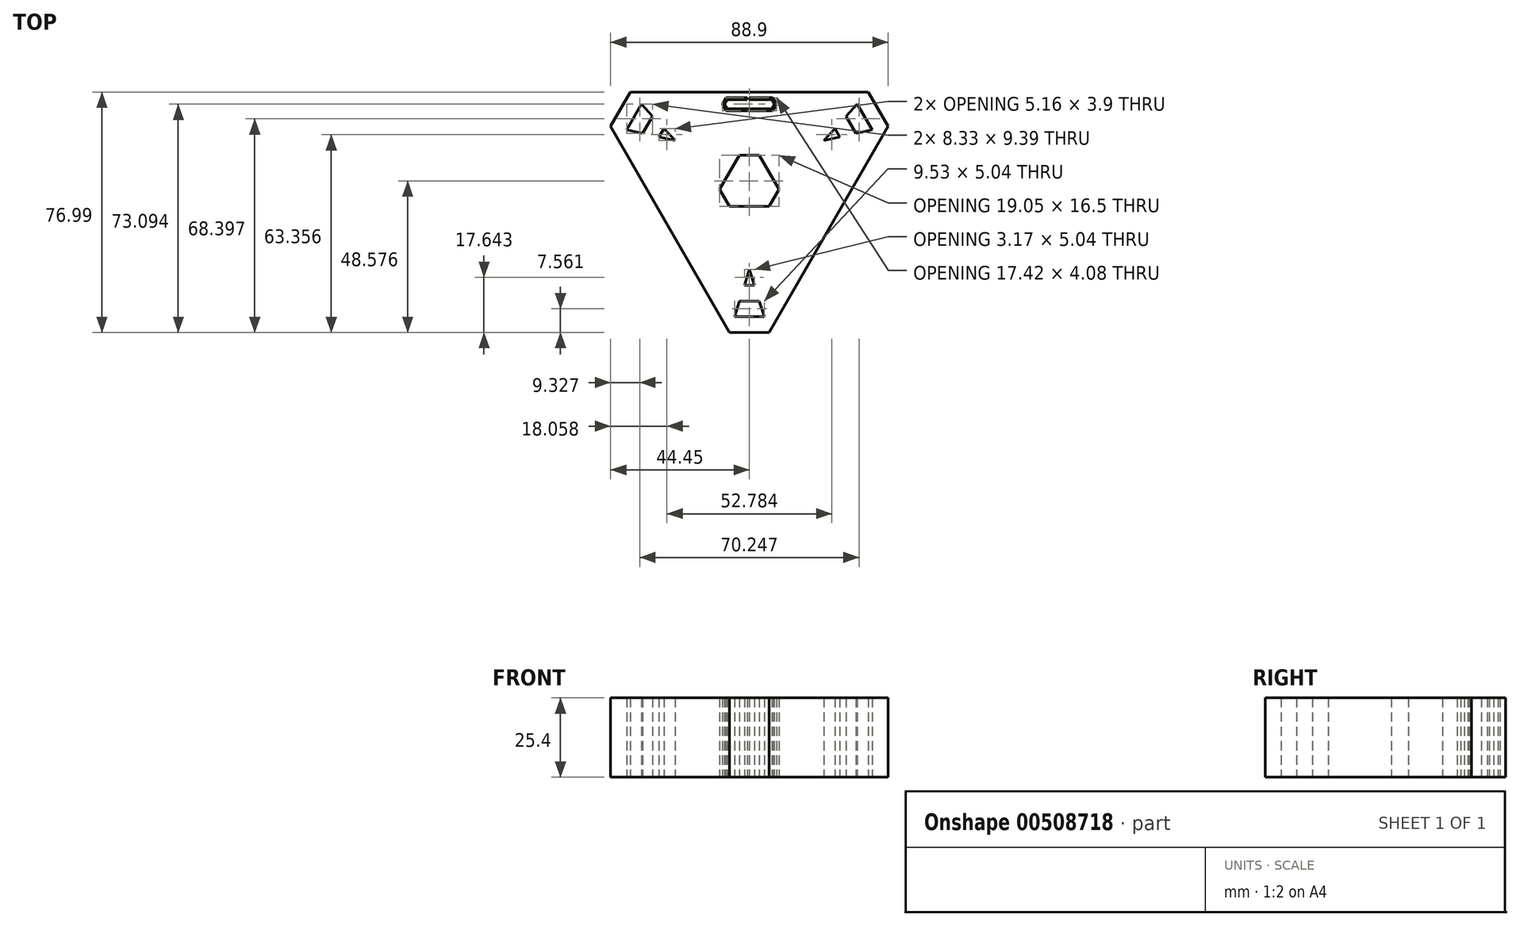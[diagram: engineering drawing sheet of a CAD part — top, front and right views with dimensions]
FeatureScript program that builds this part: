
annotation { "Feature Type Name" : "Feature", "Feature Type Description" : "" }
export const myFeature = defineFeature(function(context is Context, id is Id, definition is map)
    precondition{}
    {
        {
            var Q0;
            Q0=qCreatedBy(makeId("Top.planeOp"),FACE);
            var sketch = newSketch(context, id + "F0", { "sketchPlane" : qUnion([Q0])});
            skCircle(sketch, "E0.cCircle", {"center": v(0, 0) * mm, "radius": 29.33 * mm, "construction": true});
            skLineSegment(sketch, "E0.0", {"start": v(-50.8, 29.33) * mm, "end": v(50.8, 29.33) * mm, "construction": true});
            skLineSegment(sketch, "E0.1", {"start": v(50.8, 29.33) * mm, "end": v(0, -58.66) * mm, "construction": true});
            skLineSegment(sketch, "E0.2", {"start": v(0, -58.66) * mm, "end": v(-50.8, 29.33) * mm, "construction": true});
            skPoint(sketch, "E0.0.midPoint", {"position": v(0, 29.33) * mm});
            skPoint(sketch, "E1", {"position": v(-25.4, -14.66) * mm});
            skPoint(sketch, "E2", {"position": v(25.4, -14.66) * mm});
            skSolve(sketch);
        }
        {
            var Q0;
            Q0=qCreatedBy(makeId("Top.planeOp"),FACE);
            var sketch = newSketch(context, id + "F1", { "sketchPlane" : qUnion([Q0])});
            skPoint(sketch, "E3.0", {"position": v(0, 29.33) * mm});
            skPoint(sketch, "E4.0", {"position": v(-50.8, 29.33) * mm});
            skPoint(sketch, "E5.0", {"position": v(-25.4, -14.66) * mm});
            skPoint(sketch, "E6.0", {"position": v(25.4, -14.66) * mm});
            skPoint(sketch, "E7.0", {"position": v(50.8, 29.33) * mm});
            skPoint(sketch, "E8.0", {"position": v(0, -58.66) * mm});
            skLineSegment(sketch, "E9", {"start": v(-50.8, 29.33) * mm, "end": v(0, 29.33) * mm, "construction": true});
            skLineSegment(sketch, "E10", {"start": v(-50.8, 29.33) * mm, "end": v(-25.4, -14.66) * mm, "construction": true});
            skLineSegment(sketch, "E11", {"start": v(-25.4, -14.66) * mm, "end": v(0, 29.33) * mm, "construction": true});
            skLineSegment(sketch, "E12", {"start": v(0, 29.33) * mm, "end": v(50.8, 29.33) * mm, "construction": true});
            skLineSegment(sketch, "E13", {"start": v(50.8, 29.33) * mm, "end": v(25.4, -14.66) * mm, "construction": true});
            skLineSegment(sketch, "E14", {"start": v(25.4, -14.66) * mm, "end": v(0, 29.33) * mm, "construction": true});
            skLineSegment(sketch, "E15", {"start": v(0, -58.66) * mm, "end": v(-25.4, -14.66) * mm, "construction": true});
            skLineSegment(sketch, "E16", {"start": v(-25.4, -14.66) * mm, "end": v(25.4, -14.66) * mm, "construction": true});
            skLineSegment(sketch, "E17", {"start": v(25.4, -14.66) * mm, "end": v(0, -58.66) * mm, "construction": true});
            skPoint(sketch, "E18", {"position": v(-25.4, 29.33) * mm});
            skPoint(sketch, "E19", {"position": v(-38.1, 7.33) * mm});
            skPoint(sketch, "E20", {"position": v(-12.7, 7.33) * mm});
            skPoint(sketch, "E21", {"position": v(12.7, 7.33) * mm});
            skPoint(sketch, "E22", {"position": v(38.1, 7.33) * mm});
            skPoint(sketch, "E23", {"position": v(25.4, 29.33) * mm});
            skPoint(sketch, "E24", {"position": v(0, -14.66) * mm});
            skPoint(sketch, "E25", {"position": v(-12.7, -36.66) * mm});
            skPoint(sketch, "E26", {"position": v(12.7, -36.66) * mm});
            skSolve(sketch);
        }
        {
            var Q0;
            Q0=qCreatedBy(makeId("Top.planeOp"),FACE);
            var sketch = newSketch(context, id + "F2", { "sketchPlane" : qUnion([Q0])});
            skPoint(sketch, "E27.0", {"position": v(-25.4, 29.33) * mm});
            skPoint(sketch, "E28.0", {"position": v(-38.1, 7.33) * mm});
            skPoint(sketch, "E29.0", {"position": v(-50.8, 29.33) * mm});
            skPoint(sketch, "E30.0", {"position": v(25.4, 29.33) * mm});
            skPoint(sketch, "E31.0", {"position": v(50.8, 29.33) * mm});
            skPoint(sketch, "E32.0", {"position": v(38.1, 7.33) * mm});
            skPoint(sketch, "E33.0", {"position": v(12.7, -36.66) * mm});
            skPoint(sketch, "E34.0", {"position": v(-12.7, -36.66) * mm});
            skPoint(sketch, "E35.0", {"position": v(0, -58.66) * mm});
            skLineSegment(sketch, "E36", {"start": v(-38.1, 7.33) * mm, "end": v(-25.4, 29.33) * mm, "construction": true});
            skLineSegment(sketch, "E37", {"start": v(-50.8, 29.33) * mm, "end": v(-25.4, 29.33) * mm, "construction": true});
            skLineSegment(sketch, "E38", {"start": v(-50.8, 29.33) * mm, "end": v(-38.1, 7.33) * mm, "construction": true});
            skLineSegment(sketch, "E39", {"start": v(25.4, 29.33) * mm, "end": v(50.8, 29.33) * mm, "construction": true});
            skLineSegment(sketch, "E40", {"start": v(50.8, 29.33) * mm, "end": v(38.1, 7.33) * mm, "construction": true});
            skLineSegment(sketch, "E41", {"start": v(38.1, 7.33) * mm, "end": v(25.4, 29.33) * mm, "construction": true});
            skLineSegment(sketch, "E42", {"start": v(-12.7, -36.66) * mm, "end": v(0, -58.66) * mm, "construction": true});
            skLineSegment(sketch, "E43", {"start": v(12.7, -36.66) * mm, "end": v(-12.7, -36.66) * mm, "construction": true});
            skLineSegment(sketch, "E44", {"start": v(0, -58.66) * mm, "end": v(12.7, -36.66) * mm, "construction": true});
            skPoint(sketch, "E45", {"position": v(-6.35, -47.66) * mm});
            skPoint(sketch, "E46", {"position": v(0, -36.66) * mm});
            skPoint(sketch, "E47", {"position": v(6.35, -47.66) * mm});
            skPoint(sketch, "E48", {"position": v(-44.45, 18.33) * mm});
            skPoint(sketch, "E49", {"position": v(-31.75, 18.33) * mm});
            skPoint(sketch, "E50", {"position": v(-38.1, 29.33) * mm});
            skPoint(sketch, "E51", {"position": v(31.75, 18.33) * mm});
            skPoint(sketch, "E52", {"position": v(38.1, 29.33) * mm});
            skPoint(sketch, "E53", {"position": v(44.45, 18.33) * mm});
            skSolve(sketch);
        }
        {
            var Q0;
            Q0=qCreatedBy(makeId("Top.planeOp"),FACE);
            var sketch = newSketch(context, id + "F3", { "sketchPlane" : qUnion([Q0])});
            skPoint(sketch, "E54.0", {"position": v(-38.1, 29.33) * mm});
            skPoint(sketch, "E55.0", {"position": v(-44.45, 18.33) * mm});
            skPoint(sketch, "E56.0", {"position": v(38.1, 29.33) * mm});
            skPoint(sketch, "E57.0", {"position": v(44.45, 18.33) * mm});
            skPoint(sketch, "E58.0", {"position": v(-6.35, -47.66) * mm});
            skPoint(sketch, "E59.0", {"position": v(6.35, -47.66) * mm});
            skLineSegment(sketch, "E60", {"start": v(-38.1, 29.33) * mm, "end": v(38.1, 29.33) * mm});
            skLineSegment(sketch, "E61", {"start": v(38.1, 29.33) * mm, "end": v(44.45, 18.33) * mm});
            skLineSegment(sketch, "E62", {"start": v(44.45, 18.33) * mm, "end": v(6.35, -47.66) * mm});
            skLineSegment(sketch, "E63", {"start": v(6.35, -47.66) * mm, "end": v(-6.35, -47.66) * mm});
            skLineSegment(sketch, "E64", {"start": v(-6.35, -47.66) * mm, "end": v(-44.45, 18.33) * mm});
            skLineSegment(sketch, "E65", {"start": v(-44.45, 18.33) * mm, "end": v(-38.1, 29.33) * mm});
            skSolve(sketch);
        }
        {
            var Q0;
            Q0 = qSketchRegion(id + "F3", true);
            extrude(context, id + "F4", {"entities" : qUnion([Q0]), "depth" : 25.4 * mm, "offsetDistance" : 25.4 * mm});
        }
        {
            var Q0;
            Q0=qCreatedBy(makeId("Top.planeOp"),FACE);
            var sketch = newSketch(context, id + "F5", { "sketchPlane" : qUnion([Q0])});
            skPoint(sketch, "E66.0", {"position": v(0, 0) * mm});
            skPoint(sketch, "E67.0", {"position": v(0, -14.66) * mm});
            skLineSegment(sketch, "E68", {"start": v(0, -14.66) * mm, "end": v(0, 0) * mm, "construction": true});
            skLineSegment(sketch, "E69", {"start": v(0, 0) * mm, "end": v(0, 14.66) * mm, "construction": true});
            skPoint(sketch, "E70", {"position": v(0, 14.66) * mm});
            skCircle(sketch, "E71.cCircle", {"center": v(0, 0) * mm, "radius": 14.66 * mm, "construction": true});
            skLineSegment(sketch, "E71.0", {"start": v(0, 14.66) * mm, "end": v(12.7, -7.33) * mm, "construction": true});
            skLineSegment(sketch, "E71.1", {"start": v(12.7, -7.33) * mm, "end": v(-12.7, -7.33) * mm, "construction": true});
            skLineSegment(sketch, "E71.2", {"start": v(-12.7, -7.33) * mm, "end": v(0, 14.66) * mm, "construction": true});
            skPoint(sketch, "E72", {"position": v(-6.35, 3.67) * mm});
            skPoint(sketch, "E73", {"position": v(6.35, 3.67) * mm});
            skPoint(sketch, "E74", {"position": v(0, -7.33) * mm});
            skSolve(sketch);
        }
        {
            var Q0;
            Q0=qCreatedBy(makeId("Top.planeOp"),FACE);
            var sketch = newSketch(context, id + "F6", { "sketchPlane" : qUnion([Q0])});
            skPoint(sketch, "E75.0", {"position": v(-6.35, 3.67) * mm});
            skPoint(sketch, "E76.0", {"position": v(-12.7, -7.33) * mm});
            skPoint(sketch, "E77.0", {"position": v(0, -7.33) * mm});
            skPoint(sketch, "E78.0", {"position": v(12.7, -7.33) * mm});
            skPoint(sketch, "E79.0", {"position": v(6.35, 3.67) * mm});
            skPoint(sketch, "E80.0", {"position": v(0, 14.66) * mm});
            skLineSegment(sketch, "E81", {"start": v(-6.35, 3.67) * mm, "end": v(-12.7, -7.33) * mm, "construction": true});
            skLineSegment(sketch, "E82", {"start": v(-12.7, -7.33) * mm, "end": v(0, -7.33) * mm, "construction": true});
            skLineSegment(sketch, "E83", {"start": v(0, -7.33) * mm, "end": v(12.7, -7.33) * mm, "construction": true});
            skLineSegment(sketch, "E84", {"start": v(12.7, -7.33) * mm, "end": v(6.35, 3.67) * mm, "construction": true});
            skLineSegment(sketch, "E85", {"start": v(6.35, 3.67) * mm, "end": v(0, 14.66) * mm, "construction": true});
            skLineSegment(sketch, "E86", {"start": v(0, 14.66) * mm, "end": v(-6.35, 3.67) * mm, "construction": true});
            skPoint(sketch, "E87", {"position": v(-3.17, 9.17) * mm});
            skPoint(sketch, "E88", {"position": v(3.17, 9.17) * mm});
            skPoint(sketch, "E89", {"position": v(9.52, -1.83) * mm});
            skPoint(sketch, "E90", {"position": v(6.35, -7.33) * mm});
            skPoint(sketch, "E91", {"position": v(-6.35, -7.33) * mm});
            skPoint(sketch, "E92", {"position": v(-9.52, -1.83) * mm});
            skSolve(sketch);
        }
        {
            var Q0;
            Q0=qCreatedBy(makeId("Top.planeOp"),FACE);
            var sketch = newSketch(context, id + "F7", { "sketchPlane" : qUnion([Q0])});
            skPoint(sketch, "E93.0", {"position": v(-3.17, 9.17) * mm});
            skPoint(sketch, "E94.0", {"position": v(3.17, 9.17) * mm});
            skPoint(sketch, "E95.0", {"position": v(9.52, -1.83) * mm});
            skPoint(sketch, "E96.0", {"position": v(6.35, -7.33) * mm});
            skPoint(sketch, "E97.0", {"position": v(-6.35, -7.33) * mm});
            skPoint(sketch, "E98.0", {"position": v(-9.52, -1.83) * mm});
            skLineSegment(sketch, "E99", {"start": v(-9.52, -1.83) * mm, "end": v(-3.17, 9.17) * mm});
            skLineSegment(sketch, "E100", {"start": v(-3.17, 9.17) * mm, "end": v(3.17, 9.17) * mm});
            skLineSegment(sketch, "E101", {"start": v(9.52, -1.83) * mm, "end": v(6.35, -7.33) * mm});
            skLineSegment(sketch, "E102", {"start": v(9.52, -1.83) * mm, "end": v(3.17, 9.17) * mm});
            skLineSegment(sketch, "E103", {"start": v(-9.52, -1.83) * mm, "end": v(-6.35, -7.33) * mm});
            skLineSegment(sketch, "E104", {"start": v(-6.35, -7.33) * mm, "end": v(6.35, -7.33) * mm});
            skSolve(sketch);
        }
        {
            var Q0;
            Q0 = qSketchRegion(id + "F7", true);
            extrude(context, id + "F8", {"entities" : qUnion([Q0]), "operationType" : NewBodyOperationType.REMOVE, "endBound" : BoundingType.THROUGH_ALL, "depth" : 25.4 * mm, "offsetDistance" : 25.4 * mm});
        }
        {
            var Q0;
            Q0=qCreatedBy(makeId("Top.planeOp"),FACE);
            var sketch = newSketch(context, id + "F9", { "sketchPlane" : qUnion([Q0])});
            skPoint(sketch, "E105.0", {"position": v(-44.45, 18.33) * mm});
            skPoint(sketch, "E106.0", {"position": v(-9.52, -1.83) * mm});
            skPoint(sketch, "E107.0", {"position": v(-3.17, 9.17) * mm});
            skPoint(sketch, "E108.0", {"position": v(-38.1, 29.33) * mm});
            skPoint(sketch, "E109.0", {"position": v(38.1, 29.33) * mm});
            skPoint(sketch, "E110.0", {"position": v(44.45, 18.33) * mm});
            skPoint(sketch, "E111.0", {"position": v(9.53, -1.83) * mm});
            skPoint(sketch, "E112.0", {"position": v(3.17, 9.17) * mm});
            skPoint(sketch, "E113.0", {"position": v(6.35, -7.33) * mm});
            skPoint(sketch, "E114.0", {"position": v(-6.35, -7.33) * mm});
            skPoint(sketch, "E115.0", {"position": v(-6.35, -47.66) * mm});
            skPoint(sketch, "E116.0", {"position": v(6.35, -47.66) * mm});
            skLineSegment(sketch, "E117", {"start": v(-38.1, 29.33) * mm, "end": v(-30.96, 21.54) * mm, "construction": true});
            skLineSegment(sketch, "E118", {"start": v(-23.81, 13.75) * mm, "end": v(-9.52, -1.83) * mm, "construction": true});
            skLineSegment(sketch, "E119", {"start": v(-44.45, 18.33) * mm, "end": v(-34.13, 16.04) * mm, "construction": true});
            skLineSegment(sketch, "E120", {"start": v(-3.17, 9.17) * mm, "end": v(-23.81, 13.75) * mm, "construction": true});
            skLineSegment(sketch, "E121", {"start": v(9.53, -1.83) * mm, "end": v(23.81, 13.75) * mm, "construction": true});
            skLineSegment(sketch, "E122", {"start": v(-6.35, -7.33) * mm, "end": v(0, -27.5) * mm, "construction": true});
            skLineSegment(sketch, "E123", {"start": v(23.81, 13.75) * mm, "end": v(30.96, 21.54) * mm, "construction": true});
            skLineSegment(sketch, "E124", {"start": v(0, -27.5) * mm, "end": v(3.18, -37.58) * mm, "construction": true});
            skLineSegment(sketch, "E125", {"start": v(-6.35, -47.66) * mm, "end": v(-3.17, -37.58) * mm, "construction": true});
            skLineSegment(sketch, "E126", {"start": v(6.35, -7.33) * mm, "end": v(0, -27.5) * mm, "construction": true});
            skLineSegment(sketch, "E127", {"start": v(3.18, 9.17) * mm, "end": v(23.81, 13.75) * mm, "construction": true});
            skLineSegment(sketch, "E128", {"start": v(23.81, 13.75) * mm, "end": v(34.13, 16.04) * mm, "construction": true});
            skLineSegment(sketch, "E129", {"start": v(30.96, 21.54) * mm, "end": v(38.1, 29.33) * mm, "construction": true});
            skLineSegment(sketch, "E130", {"start": v(34.13, 16.04) * mm, "end": v(44.45, 18.33) * mm, "construction": true});
            skLineSegment(sketch, "E131", {"start": v(-30.96, 21.54) * mm, "end": v(-23.81, 13.75) * mm, "construction": true});
            skLineSegment(sketch, "E132", {"start": v(-34.13, 16.04) * mm, "end": v(-23.81, 13.75) * mm, "construction": true});
            skLineSegment(sketch, "E133", {"start": v(-3.17, -37.58) * mm, "end": v(0, -27.5) * mm, "construction": true});
            skLineSegment(sketch, "E134", {"start": v(3.18, -37.58) * mm, "end": v(6.35, -47.66) * mm, "construction": true});
            skPoint(sketch, "E135", {"position": v(-1.59, -32.54) * mm});
            skPoint(sketch, "E136", {"position": v(-4.76, -42.62) * mm});
            skPoint(sketch, "E137", {"position": v(1.59, -32.54) * mm});
            skPoint(sketch, "E138", {"position": v(4.76, -42.62) * mm});
            skPoint(sketch, "E139", {"position": v(-34.53, 25.43) * mm});
            skPoint(sketch, "E140", {"position": v(-27.38, 17.64) * mm});
            skPoint(sketch, "E141", {"position": v(-39.3, 17.19) * mm});
            skPoint(sketch, "E142", {"position": v(-28.97, 14.9) * mm});
            skPoint(sketch, "E143", {"position": v(27.38, 17.64) * mm});
            skPoint(sketch, "E144", {"position": v(34.53, 25.43) * mm});
            skPoint(sketch, "E145", {"position": v(28.97, 14.9) * mm});
            skPoint(sketch, "E146", {"position": v(39.3, 17.19) * mm});
            skLineSegment(sketch, "E147", {"start": v(34.53, 25.43) * mm, "end": v(39.3, 17.19) * mm});
            skLineSegment(sketch, "E148", {"start": v(39.3, 17.19) * mm, "end": v(34.13, 16.04) * mm});
            skLineSegment(sketch, "E149", {"start": v(34.13, 16.04) * mm, "end": v(30.96, 21.54) * mm});
            skLineSegment(sketch, "E150", {"start": v(30.96, 21.54) * mm, "end": v(34.53, 25.43) * mm});
            skLineSegment(sketch, "E151", {"start": v(27.38, 17.64) * mm, "end": v(23.81, 13.75) * mm});
            skLineSegment(sketch, "E152", {"start": v(28.97, 14.9) * mm, "end": v(23.81, 13.75) * mm});
            skLineSegment(sketch, "E153", {"start": v(27.38, 17.64) * mm, "end": v(28.97, 14.9) * mm});
            skLineSegment(sketch, "E154", {"start": v(-34.53, 25.43) * mm, "end": v(-39.3, 17.19) * mm});
            skLineSegment(sketch, "E155", {"start": v(-28.97, 14.9) * mm, "end": v(-27.38, 17.64) * mm});
            skLineSegment(sketch, "E156", {"start": v(-30.96, 21.54) * mm, "end": v(-34.13, 16.04) * mm});
            skLineSegment(sketch, "E157", {"start": v(-39.3, 17.19) * mm, "end": v(-34.13, 16.04) * mm});
            skLineSegment(sketch, "E158", {"start": v(-28.97, 14.9) * mm, "end": v(-23.81, 13.75) * mm});
            skLineSegment(sketch, "E159", {"start": v(-27.38, 17.64) * mm, "end": v(-23.81, 13.75) * mm});
            skLineSegment(sketch, "E160", {"start": v(-34.53, 25.43) * mm, "end": v(-30.96, 21.54) * mm});
            skLineSegment(sketch, "E161", {"start": v(-1.59, -32.54) * mm, "end": v(0, -27.5) * mm});
            skLineSegment(sketch, "E162", {"start": v(0, -27.5) * mm, "end": v(1.59, -32.54) * mm});
            skLineSegment(sketch, "E163", {"start": v(1.59, -32.54) * mm, "end": v(-1.59, -32.54) * mm});
            skLineSegment(sketch, "E164", {"start": v(-3.17, -37.58) * mm, "end": v(-4.76, -42.62) * mm});
            skLineSegment(sketch, "E165", {"start": v(-4.76, -42.62) * mm, "end": v(4.76, -42.62) * mm});
            skLineSegment(sketch, "E166", {"start": v(4.76, -42.62) * mm, "end": v(3.18, -37.58) * mm});
            skLineSegment(sketch, "E167", {"start": v(3.18, -37.58) * mm, "end": v(-3.17, -37.58) * mm});
            skLineSegment(sketch, "E168", {"start": v(-34.53, 25.43) * mm, "end": v(34.53, 25.43) * mm, "construction": true});
            skPoint(sketch, "E169", {"position": v(0, 25.43) * mm});
            skPoint(sketch, "E170", {"position": v(6.35, 25.43) * mm});
            skCircle(sketch, "E171.cCircle", {"center": v(6.35, 25.43) * mm, "radius": 1.63 * mm, "construction": true});
            skLineSegment(sketch, "E171.0", {"start": v(7.97, 25.43) * mm, "end": v(7.16, 24.03) * mm, "construction": true});
            skLineSegment(sketch, "E171.1", {"start": v(7.16, 24.03) * mm, "end": v(5.54, 24.03) * mm, "construction": true});
            skLineSegment(sketch, "E171.2", {"start": v(5.54, 24.03) * mm, "end": v(4.73, 25.43) * mm, "construction": true});
            skLineSegment(sketch, "E171.3", {"start": v(4.73, 25.43) * mm, "end": v(5.54, 26.84) * mm, "construction": true});
            skLineSegment(sketch, "E171.4", {"start": v(5.54, 26.84) * mm, "end": v(7.16, 26.84) * mm, "construction": true});
            skLineSegment(sketch, "E171.5", {"start": v(7.16, 26.84) * mm, "end": v(7.98, 25.43) * mm, "construction": true});
            skLineSegment(sketch, "E172", {"start": v(0, 25.43) * mm, "end": v(0, 26.84) * mm, "construction": true});
            skCircle(sketch, "E173.MirrorC", {"center": v(-6.35, 25.43) * mm, "radius": 1.63 * mm, "construction": true});
            skLineSegment(sketch, "E174.MirrorCS", {"start": v(-5.54, 24.03) * mm, "end": v(-4.72, 25.43) * mm, "construction": true});
            skLineSegment(sketch, "E175.MirrorCS", {"start": v(-7.16, 26.84) * mm, "end": v(-7.98, 25.43) * mm, "construction": true});
            skLineSegment(sketch, "E176.MirrorCS", {"start": v(-5.54, 26.84) * mm, "end": v(-7.16, 26.84) * mm, "construction": true});
            skLineSegment(sketch, "E177.MirrorCS", {"start": v(-7.98, 25.43) * mm, "end": v(-7.16, 24.03) * mm, "construction": true});
            skLineSegment(sketch, "E178.MirrorCS", {"start": v(-7.16, 24.03) * mm, "end": v(-5.54, 24.03) * mm, "construction": true});
            skLineSegment(sketch, "E179.MirrorCS", {"start": v(-4.73, 25.43) * mm, "end": v(-5.54, 26.84) * mm, "construction": true});
            skLineSegment(sketch, "E180", {"start": v(-7.98, 25.43) * mm, "end": v(-7.16, 26.84) * mm});
            skLineSegment(sketch, "E181", {"start": v(-7.16, 26.84) * mm, "end": v(-0.63, 26.84) * mm});
            skLineSegment(sketch, "E182", {"start": v(7.16, 26.84) * mm, "end": v(7.98, 25.43) * mm});
            skLineSegment(sketch, "E183", {"start": v(7.98, 25.43) * mm, "end": v(7.16, 24.03) * mm});
            skLineSegment(sketch, "E184", {"start": v(7.16, 24.03) * mm, "end": v(-7.16, 24.03) * mm});
            skLineSegment(sketch, "E185", {"start": v(-7.16, 24.03) * mm, "end": v(-7.98, 25.43) * mm});
            skLineSegment(sketch, "E186", {"start": v(30.96, 21.54) * mm, "end": v(-30.96, 21.54) * mm, "construction": true});
            skLineSegment(sketch, "E187.0", {"start": v(-7.53, 27.48) * mm, "end": v(-8.7, 25.43) * mm});
            skLineSegment(sketch, "E187.1", {"start": v(7.53, 27.48) * mm, "end": v(8.7, 25.43) * mm});
            skLineSegment(sketch, "E187.2", {"start": v(8.7, 25.43) * mm, "end": v(7.53, 23.4) * mm});
            skLineSegment(sketch, "E187.3", {"start": v(-7.53, 27.48) * mm, "end": v(7.53, 27.48) * mm});
            skLineSegment(sketch, "E187.4", {"start": v(7.53, 23.4) * mm, "end": v(-7.53, 23.4) * mm});
            skLineSegment(sketch, "E187.5", {"start": v(-8.7, 25.43) * mm, "end": v(-7.53, 23.4) * mm});
            skLineSegment(sketch, "E188", {"start": v(0, 26.84) * mm, "end": v(7.16, 26.84) * mm});
            skLineSegment(sketch, "E189", {"start": v(-0.63, 26.84) * mm, "end": v(-0.63, 27.48) * mm});
            skLineSegment(sketch, "E190", {"start": v(0, 26.84) * mm, "end": v(0, 27.48) * mm});
            skSolve(sketch);
        }
        {
            var Q0;
            Q0 = qSketchRegion(id + "F9", true);
            extrude(context, id + "F10", {"entities" : qUnion([Q0]), "operationType" : NewBodyOperationType.REMOVE, "endBound" : BoundingType.THROUGH_ALL, "depth" : 25.4 * mm, "offsetDistance" : 25.4 * mm});
        }
        {
            var Q0;
            Q0=makeQuery(id+"F9.imprint","IMPRINT",FACE,{"disambiguationData":[TD([[makeQuery(id+"F9.imprint","IMPRINT",EDGE,{"derivedFrom":sQuery(id+"F9.wireOp",EDGE,"E180")}),-1.0]])]});
            extrude(context, id + "F11", {"entities" : qUnion([Q0]), "operationType" : NewBodyOperationType.ADD, "depth" : 25.4 * mm, "offsetDistance" : 25.4 * mm});
        }
    });
